# Revit family: Sink-Bradley_Corp-Omnideck_LD-3010_WashBar_Duo_2Basin
name_source: partatom
category: Plumbing Fixtures
revit_build: Autodesk Revit 2018 (Build: 20170223_1515(x64)
units: mm (PartAtom-declared; Revit-internal decimal feet)

## family parameters
Always vertical = Yes
Cut with Voids When Loaded = No
OmniClass Number = 23.45.00.00
OmniClass Title = Sanitary, Laundry, and Cleaning Equipment
Part Type = Normal
Room Calculation Point = No
Round Connector Dimension = Use Diameter
Shared = No
Work Plane-Based = No

## types (1)
- Omnideck LD-3010 WashBar Duo 2-Basin
    Assembly Code = D2010400
    Description = Bradley Omnideck Lavatory LD 3010 WashBar Duo Two-Basin
    Manufacturer = Bradley Corporation
    Manufacturer Installation URL - English = https://www.bradleycorp.com
    MasterFormat Number = 22 42 16
    MasterFormat Title = Commercial Lavatories and Sinks
    Model = Omnideck LD 3010 WB TR1 2-Basin
    OmniClass Table 23 Number = 23.45 05 14 14
    OmniClass Table 23 Title = Sinks/Lavatories
    Product Page URL = https://www.bradleycorp.com
    Product Tech Data URL - English = https://www.bradleycorp.com
    Specifications URL = https://www.bradleycorp.com
    URL = http://bradleycorp.com
    Version = 1.0

## geometry (parser evidence)
native form markers: Blend x16, Sweep x10
no freeform markers — native parametric forms only
